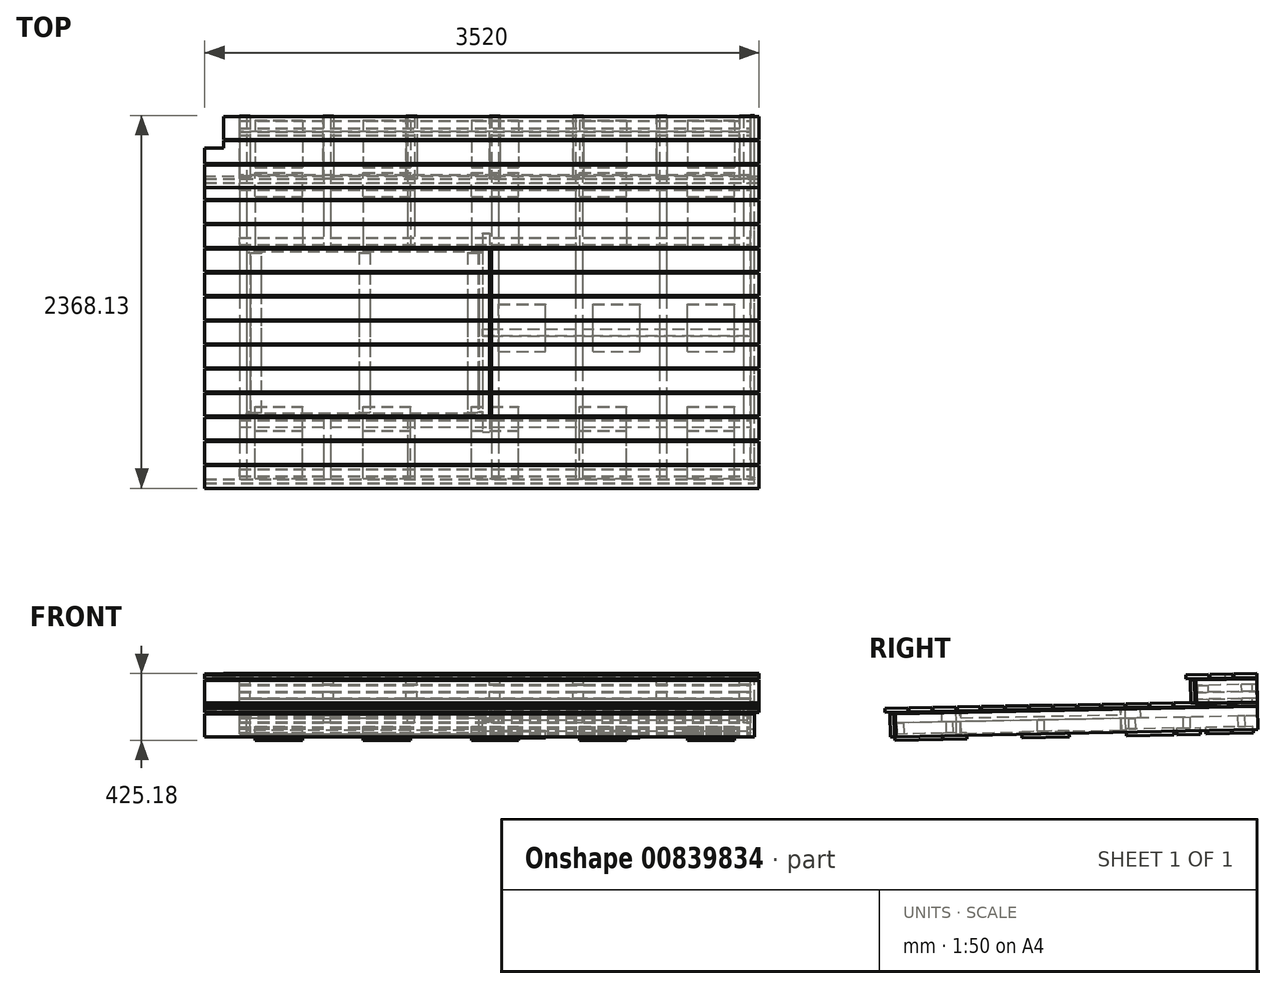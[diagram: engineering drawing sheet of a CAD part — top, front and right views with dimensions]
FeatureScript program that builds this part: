
annotation { "Feature Type Name" : "Feature", "Feature Type Description" : "" }
export const myFeature = defineFeature(function(context is Context, id is Id, definition is map)
    precondition{}
    {
        {
            var Q0;
            Q0=qCreatedBy(makeId("Top.planeOp"),FACE);
            var sketch = newSketch(context, id + "F0", { "sketchPlane" : qUnion([Q0])});
            skLineSegment(sketch, "E0", {"start": v(0, 0) * mm, "end": v(3520, 0) * mm, "construction": true});
            skSolve(sketch);
        }
        {
            var Q0;
            Q0=qCreatedBy(makeId("Top.planeOp"),FACE);
            var Q1;
            Q1=sQuery(id+"F0.wireOp",EDGE,"E0");
            cPlane(context, id + "F1", {"entities" : qUnion([Q0, Q1]), "cplaneType" : CPlaneType.LINE_ANGLE, "offset" : 25 * mm, "angle" : 1.15 * degree, "width" : 150 * mm, "height" : 150 * mm});
        }
        {
            var Q0;
            Q0=qCreatedBy(id+"F1.planeOp",FACE);
            var sketch = newSketch(context, id + "F2", { "sketchPlane" : qUnion([Q0])});
            skLineSegment(sketch, "E1.bottom", {"start": v(120, 0) * mm, "end": v(3520, 0) * mm});
            skLineSegment(sketch, "E1.top", {"start": v(120, 145) * mm, "end": v(3520, 145) * mm});
            skLineSegment(sketch, "E1.left", {"start": v(120, 0) * mm, "end": v(120, 145) * mm});
            skLineSegment(sketch, "E1.right", {"start": v(3520, 0) * mm, "end": v(3520, 145) * mm});
            skLineSegment(sketch, "E2.bottom", {"start": v(3520, 153) * mm, "end": v(120, 153) * mm});
            skLineSegment(sketch, "E2.top", {"start": v(3520, 298) * mm, "end": v(0, 298) * mm});
            skLineSegment(sketch, "E2.left", {"start": v(3520, 153) * mm, "end": v(3520, 298) * mm});
            skLineSegment(sketch, "E2.right", {"start": v(0, 200) * mm, "end": v(0, 298) * mm});
            skLineSegment(sketch, "E3.bottom", {"start": v(3520, 306) * mm, "end": v(0, 306) * mm});
            skLineSegment(sketch, "E3.top", {"start": v(3520, 451) * mm, "end": v(0, 451) * mm});
            skLineSegment(sketch, "E3.left", {"start": v(3520, 306) * mm, "end": v(3520, 451) * mm});
            skLineSegment(sketch, "E3.right", {"start": v(0, 306) * mm, "end": v(0, 451) * mm});
            skLineSegment(sketch, "E4", {"start": v(120, 153) * mm, "end": v(120, 200) * mm});
            skLineSegment(sketch, "E5", {"start": v(120, 200) * mm, "end": v(0, 200) * mm});
            skSolve(sketch);
        }
        {
            var Q0;
            Q0 = qSketchRegion(id + "F2", true);
            extrude(context, id + "F3", {"entities" : qUnion([Q0]), "depth" : 25 * mm, "offsetDistance" : 25 * mm});
        }
        {
            var Q0;
            Q0=makeQuery(id+"F3.opExtrude","CAP_FACE",FACE,{"disambiguationData":[OSD([sQuery(id+"F2.wireOp",EDGE,"E3.bottom"),sQuery(id+"F2.wireOp",EDGE,"E3.top"),sQuery(id+"F2.wireOp",EDGE,"E3.left"),sQuery(id+"F2.wireOp",EDGE,"E3.right")])],"isStart":false});
            var sketch = newSketch(context, id + "F4", { "sketchPlane" : qUnion([Q0])});
            skLineSegment(sketch, "E6.bottom", {"start": v(3465, 0) * mm, "end": v(3397, 0) * mm});
            skLineSegment(sketch, "E6.top", {"start": v(3465, 396) * mm, "end": v(3397, 396) * mm});
            skLineSegment(sketch, "E6.left", {"start": v(3465, 0) * mm, "end": v(3465, 396) * mm});
            skLineSegment(sketch, "E6.right", {"start": v(3397, 0) * mm, "end": v(3397, 396) * mm});
            skLineSegment(sketch, "E7.1.0.0", {"start": v(2935.5, 396) * mm, "end": v(2867.5, 396) * mm});
            skLineSegment(sketch, "E7.1.0.1", {"start": v(2935.5, 0) * mm, "end": v(2935.5, 396) * mm});
            skLineSegment(sketch, "E7.1.0.2", {"start": v(2867.5, 0) * mm, "end": v(2867.5, 396) * mm});
            skLineSegment(sketch, "E7.1.0.3", {"start": v(2935.5, 0) * mm, "end": v(2867.5, 0) * mm});
            skLineSegment(sketch, "E7.2.0.0", {"start": v(2406, 396) * mm, "end": v(2338, 396) * mm});
            skLineSegment(sketch, "E7.2.0.1", {"start": v(2406, 0) * mm, "end": v(2406, 396) * mm});
            skLineSegment(sketch, "E7.2.0.2", {"start": v(2338, 0) * mm, "end": v(2338, 396) * mm});
            skLineSegment(sketch, "E7.2.0.3", {"start": v(2406, 0) * mm, "end": v(2338, 0) * mm});
            skLineSegment(sketch, "E7.direction1", {"start": v(3397, 0) * mm, "end": v(2867.5, 0) * mm, "construction": true});
            skLineSegment(sketch, "E8.0.3.0", {"start": v(1876.5, 396) * mm, "end": v(1808.5, 396) * mm});
            skLineSegment(sketch, "E8.3.3.0", {"start": v(1876.5, 0) * mm, "end": v(1876.5, 396) * mm});
            skLineSegment(sketch, "E8.6.3.0", {"start": v(1808.5, 0) * mm, "end": v(1808.5, 396) * mm});
            skLineSegment(sketch, "E8.9.3.0", {"start": v(1876.5, 0) * mm, "end": v(1808.5, 0) * mm});
            skLineSegment(sketch, "E8.0.4.0", {"start": v(1347, 396) * mm, "end": v(1279, 396) * mm});
            skLineSegment(sketch, "E8.3.4.0", {"start": v(1347, 0) * mm, "end": v(1347, 396) * mm});
            skLineSegment(sketch, "E8.6.4.0", {"start": v(1279, 0) * mm, "end": v(1279, 396) * mm});
            skLineSegment(sketch, "E8.9.4.0", {"start": v(1347, 0) * mm, "end": v(1279, 0) * mm});
            skLineSegment(sketch, "E9.0.5.0", {"start": v(817.5, 396) * mm, "end": v(749.5, 396) * mm});
            skLineSegment(sketch, "E9.3.5.0", {"start": v(817.5, 0) * mm, "end": v(817.5, 396) * mm});
            skLineSegment(sketch, "E9.6.5.0", {"start": v(749.5, 0) * mm, "end": v(749.5, 396) * mm});
            skLineSegment(sketch, "E9.9.5.0", {"start": v(817.5, 0) * mm, "end": v(749.5, 0) * mm});
            skLineSegment(sketch, "E10.0.6.0", {"start": v(288, 396) * mm, "end": v(220, 396) * mm});
            skLineSegment(sketch, "E10.3.6.0", {"start": v(288, 0) * mm, "end": v(288, 396) * mm});
            skLineSegment(sketch, "E10.6.6.0", {"start": v(220, 0) * mm, "end": v(220, 396) * mm});
            skLineSegment(sketch, "E10.9.6.0", {"start": v(288, 0) * mm, "end": v(220, 0) * mm});
            skSolve(sketch);
        }
        {
            var Q0;
            Q0 = qSketchRegion(id + "F4", true);
            extrude(context, id + "F5", {"entities" : qUnion([Q0]), "depth" : 44 * mm, "offsetDistance" : 25 * mm});
        }
        {
            var Q0;
            Q0=makeQuery(id+"F5.opExtrude","CAP_FACE",FACE,{"disambiguationData":[OSD([sQuery(id+"F4.wireOp",EDGE,"E6.bottom"),sQuery(id+"F4.wireOp",EDGE,"E6.top"),sQuery(id+"F4.wireOp",EDGE,"E6.left"),sQuery(id+"F4.wireOp",EDGE,"E6.right")])],"isStart":false});
            var sketch = newSketch(context, id + "F6", { "sketchPlane" : qUnion([Q0])});
            skLineSegment(sketch, "E11.bottom", {"start": v(220, 30) * mm, "end": v(3465, 30) * mm});
            skLineSegment(sketch, "E11.top", {"start": v(220, 98) * mm, "end": v(3465, 98) * mm});
            skLineSegment(sketch, "E11.left", {"start": v(220, 30) * mm, "end": v(220, 98) * mm});
            skLineSegment(sketch, "E11.right", {"start": v(3465, 30) * mm, "end": v(3465, 98) * mm});
            skLineSegment(sketch, "E12.bottom", {"start": v(220, 376) * mm, "end": v(3465, 376) * mm});
            skLineSegment(sketch, "E12.top", {"start": v(220, 308) * mm, "end": v(3465, 308) * mm});
            skLineSegment(sketch, "E12.left", {"start": v(220, 376) * mm, "end": v(220, 308) * mm});
            skLineSegment(sketch, "E12.right", {"start": v(3465, 376) * mm, "end": v(3465, 308) * mm});
            skSolve(sketch);
        }
        {
            var Q0;
            Q0 = qSketchRegion(id + "F6", true);
            extrude(context, id + "F7", {"entities" : qUnion([Q0]), "depth" : 44 * mm, "offsetDistance" : 25 * mm});
        }
        {
            var Q0;
            Q0=makeQuery(id+"F7.opExtrude","CAP_FACE",FACE,{"disambiguationData":[OSD([sQuery(id+"F6.wireOp",EDGE,"E11.bottom"),sQuery(id+"F6.wireOp",EDGE,"E11.top"),sQuery(id+"F6.wireOp",EDGE,"E11.left"),sQuery(id+"F6.wireOp",EDGE,"E11.right")])],"isStart":false});
            var sketch = newSketch(context, id + "F8", { "sketchPlane" : qUnion([Q0])});
            skLineSegment(sketch, "E13.0.0", {"start": v(2867.5, 396) * mm, "end": v(2867.5, 0) * mm});
            skLineSegment(sketch, "E13.0.1", {"start": v(2867.5, 0) * mm, "end": v(2935.5, 0) * mm});
            skLineSegment(sketch, "E13.0.2", {"start": v(2935.5, 0) * mm, "end": v(2935.5, 396) * mm});
            skLineSegment(sketch, "E13.0.3", {"start": v(2935.5, 396) * mm, "end": v(2867.5, 396) * mm});
            skLineSegment(sketch, "E14.0.0", {"start": v(2338, 396) * mm, "end": v(2338, 0) * mm});
            skLineSegment(sketch, "E14.0.1", {"start": v(2338, 0) * mm, "end": v(2406, 0) * mm});
            skLineSegment(sketch, "E14.0.2", {"start": v(2406, 0) * mm, "end": v(2406, 396) * mm});
            skLineSegment(sketch, "E14.0.3", {"start": v(2406, 396) * mm, "end": v(2338, 396) * mm});
            skLineSegment(sketch, "E15.0.0", {"start": v(1808.5, 396) * mm, "end": v(1808.5, 0) * mm});
            skLineSegment(sketch, "E15.0.1", {"start": v(1808.5, 0) * mm, "end": v(1876.5, 0) * mm});
            skLineSegment(sketch, "E15.0.2", {"start": v(1876.5, 0) * mm, "end": v(1876.5, 396) * mm});
            skLineSegment(sketch, "E15.0.3", {"start": v(1876.5, 396) * mm, "end": v(1808.5, 396) * mm});
            skLineSegment(sketch, "E16.0.0", {"start": v(1279, 396) * mm, "end": v(1279, 0) * mm});
            skLineSegment(sketch, "E16.0.1", {"start": v(1279, 0) * mm, "end": v(1347, 0) * mm});
            skLineSegment(sketch, "E16.0.2", {"start": v(1347, 0) * mm, "end": v(1347, 396) * mm});
            skLineSegment(sketch, "E16.0.3", {"start": v(1347, 396) * mm, "end": v(1279, 396) * mm});
            skLineSegment(sketch, "E17.0.0", {"start": v(749.5, 396) * mm, "end": v(749.5, 0) * mm});
            skLineSegment(sketch, "E17.0.1", {"start": v(749.5, 0) * mm, "end": v(817.5, 0) * mm});
            skLineSegment(sketch, "E17.0.2", {"start": v(817.5, 0) * mm, "end": v(817.5, 396) * mm});
            skLineSegment(sketch, "E17.0.3", {"start": v(817.5, 396) * mm, "end": v(749.5, 396) * mm});
            skLineSegment(sketch, "E18.0.0", {"start": v(220, 396) * mm, "end": v(220, 0) * mm});
            skLineSegment(sketch, "E18.0.1", {"start": v(220, 0) * mm, "end": v(288, 0) * mm});
            skLineSegment(sketch, "E18.0.2", {"start": v(288, 0) * mm, "end": v(288, 396) * mm});
            skLineSegment(sketch, "E18.0.3", {"start": v(288, 396) * mm, "end": v(220, 396) * mm});
            skLineSegment(sketch, "E19.0.0", {"start": v(3465, 396) * mm, "end": v(3397, 396) * mm});
            skLineSegment(sketch, "E19.0.1", {"start": v(3397, 396) * mm, "end": v(3397, 0) * mm});
            skLineSegment(sketch, "E19.0.2", {"start": v(3397, 0) * mm, "end": v(3465, 0) * mm});
            skLineSegment(sketch, "E19.0.3", {"start": v(3465, 0) * mm, "end": v(3465, 396) * mm});
            skSolve(sketch);
        }
        {
            var Q0;
            Q0 = qSketchRegion(id + "F8", true);
            extrude(context, id + "F9", {"entities" : qUnion([Q0]), "depth" : 44 * mm, "offsetDistance" : 25 * mm});
        }
        {
            var Q0;
            Q0=makeQuery(id+"F9.opExtrude","CAP_FACE",FACE,{"disambiguationData":[OSD([sQuery(id+"F8.wireOp",EDGE,"E18.0.0"),sQuery(id+"F8.wireOp",EDGE,"E18.0.1"),sQuery(id+"F8.wireOp",EDGE,"E18.0.2"),sQuery(id+"F8.wireOp",EDGE,"E18.0.3")])],"isStart":false});
            var sketch = newSketch(context, id + "F10", { "sketchPlane" : qUnion([Q0])});
            skLineSegment(sketch, "E20.0.0", {"start": v(220, 376) * mm, "end": v(220, 308) * mm});
            skLineSegment(sketch, "E20.0.1", {"start": v(220, 308) * mm, "end": v(3465, 308) * mm});
            skLineSegment(sketch, "E20.0.2", {"start": v(3465, 308) * mm, "end": v(3465, 376) * mm});
            skLineSegment(sketch, "E20.0.3", {"start": v(3465, 376) * mm, "end": v(220, 376) * mm});
            skLineSegment(sketch, "E21.0.0", {"start": v(3465, 30) * mm, "end": v(3465, 98) * mm});
            skLineSegment(sketch, "E21.0.1", {"start": v(3465, 98) * mm, "end": v(220, 98) * mm});
            skLineSegment(sketch, "E21.0.2", {"start": v(220, 98) * mm, "end": v(220, 30) * mm});
            skLineSegment(sketch, "E21.0.3", {"start": v(220, 30) * mm, "end": v(3465, 30) * mm});
            skSolve(sketch);
        }
        {
            var Q0;
            Q0 = qSketchRegion(id + "F10", true);
            extrude(context, id + "F11", {"entities" : qUnion([Q0]), "depth" : 44 * mm, "offsetDistance" : 25 * mm});
        }
        {
            var Q0;
            Q0=makeQuery(id+"F5.opExtrude","SWEPT_FACE",FACE,{"disambiguationData":[OSD([sQuery(id+"F4.wireOp",EDGE,"E10.0.6.0")])]});
            var sketch = newSketch(context, id + "F12", { "sketchPlane" : qUnion([Q0])});
            skLineSegment(sketch, "E22.bottom", {"start": v(0, -180) * mm, "end": v(3520, -180) * mm});
            skLineSegment(sketch, "E22.top", {"start": v(0, -35) * mm, "end": v(3520, -35) * mm});
            skLineSegment(sketch, "E22.left", {"start": v(0, -180) * mm, "end": v(0, -35) * mm});
            skLineSegment(sketch, "E22.right", {"start": v(3520, -180) * mm, "end": v(3520, -35) * mm});
            skSolve(sketch);
        }
        {
            var Q0;
            Q0 = qSketchRegion(id + "F12", true);
            extrude(context, id + "F13", {"entities" : qUnion([Q0]), "depth" : 25 * mm, "offsetDistance" : 25 * mm});
        }
        {
            var Q0;
            Q0=makeQuery(id+"F11.opExtrude","CAP_FACE",FACE,{"disambiguationData":[OSD([sQuery(id+"F10.wireOp",EDGE,"E21.0.0"),sQuery(id+"F10.wireOp",EDGE,"E21.0.1"),sQuery(id+"F10.wireOp",EDGE,"E21.0.2"),sQuery(id+"F10.wireOp",EDGE,"E21.0.3")])],"isStart":false});
            var sketch = newSketch(context, id + "F14", { "sketchPlane" : qUnion([Q0])});
            skLineSegment(sketch, "E23.bottom", {"start": v(3465, 0) * mm, "end": v(3421, 0) * mm});
            skLineSegment(sketch, "E23.top", {"start": v(3465, 2310) * mm, "end": v(3421, 2310) * mm});
            skLineSegment(sketch, "E23.left", {"start": v(3465, 0) * mm, "end": v(3465, 2310) * mm});
            skLineSegment(sketch, "E23.right", {"start": v(3421, 0) * mm, "end": v(3421, 2310) * mm});
            skLineSegment(sketch, "E24.1.0.0", {"start": v(2931.5, 0) * mm, "end": v(2931.5, 2310) * mm});
            skLineSegment(sketch, "E24.1.0.1", {"start": v(2887.5, 0) * mm, "end": v(2887.5, 2310) * mm});
            skLineSegment(sketch, "E24.1.0.2", {"start": v(2931.5, 2310) * mm, "end": v(2887.5, 2310) * mm});
            skLineSegment(sketch, "E24.1.0.3", {"start": v(2931.5, 0) * mm, "end": v(2887.5, 0) * mm});
            skLineSegment(sketch, "E24.2.0.0", {"start": v(2398, 0) * mm, "end": v(2398, 2310) * mm});
            skLineSegment(sketch, "E24.2.0.1", {"start": v(2354, 0) * mm, "end": v(2354, 2310) * mm});
            skLineSegment(sketch, "E24.2.0.2", {"start": v(2398, 2310) * mm, "end": v(2354, 2310) * mm});
            skLineSegment(sketch, "E24.2.0.3", {"start": v(2398, 0) * mm, "end": v(2354, 0) * mm});
            skLineSegment(sketch, "E24.3.0.0", {"start": v(1864.5, 0) * mm, "end": v(1864.5, 2310) * mm});
            skLineSegment(sketch, "E24.3.0.1", {"start": v(1820.5, 0) * mm, "end": v(1820.5, 2310) * mm});
            skLineSegment(sketch, "E24.3.0.2", {"start": v(1864.5, 2310) * mm, "end": v(1820.5, 2310) * mm});
            skLineSegment(sketch, "E24.3.0.3", {"start": v(1864.5, 0) * mm, "end": v(1820.5, 0) * mm});
            skLineSegment(sketch, "E24.4.0.0", {"start": v(1331, 0) * mm, "end": v(1331, 839) * mm});
            skLineSegment(sketch, "E24.4.0.1", {"start": v(1287, 0) * mm, "end": v(1287, 839) * mm});
            skLineSegment(sketch, "E24.4.0.2", {"start": v(1331, 2310) * mm, "end": v(1287, 2310) * mm});
            skLineSegment(sketch, "E24.4.0.3", {"start": v(1331, 0) * mm, "end": v(1287, 0) * mm});
            skLineSegment(sketch, "E24.5.0.0", {"start": v(797.5, 0) * mm, "end": v(797.5, 839) * mm});
            skLineSegment(sketch, "E24.5.0.1", {"start": v(753.5, 0) * mm, "end": v(753.5, 839) * mm});
            skLineSegment(sketch, "E24.5.0.2", {"start": v(797.5, 2310) * mm, "end": v(753.5, 2310) * mm});
            skLineSegment(sketch, "E24.5.0.3", {"start": v(797.5, 0) * mm, "end": v(753.5, 0) * mm});
            skLineSegment(sketch, "E24.6.0.0", {"start": v(264, 0) * mm, "end": v(264, 2310) * mm});
            skLineSegment(sketch, "E24.6.0.1", {"start": v(220, 0) * mm, "end": v(220, 2310) * mm});
            skLineSegment(sketch, "E24.6.0.2", {"start": v(264, 2310) * mm, "end": v(220, 2310) * mm});
            skLineSegment(sketch, "E24.6.0.3", {"start": v(264, 0) * mm, "end": v(220, 0) * mm});
            skLineSegment(sketch, "E24.direction1", {"start": v(3421, 0) * mm, "end": v(2887.5, 0) * mm, "construction": true});
            skLineSegment(sketch, "E25.bottom", {"start": v(753.5, 1914) * mm, "end": v(797.5, 1914) * mm});
            skLineSegment(sketch, "E25.top", {"start": v(753.5, 839) * mm, "end": v(797.5, 839) * mm});
            skLineSegment(sketch, "E26.trimOffspring", {"start": v(1331, 1914) * mm, "end": v(1331, 2310) * mm});
            skLineSegment(sketch, "E27.trimOffspring", {"start": v(1287, 1914) * mm, "end": v(1287, 2310) * mm});
            skLineSegment(sketch, "E28.trimOffspring", {"start": v(797.5, 1914) * mm, "end": v(797.5, 2310) * mm});
            skLineSegment(sketch, "E29.trimOffspring", {"start": v(753.5, 1914) * mm, "end": v(753.5, 2310) * mm});
            skLineSegment(sketch, "E30.trimOffspring", {"start": v(1287, 1914) * mm, "end": v(1331, 1914) * mm});
            skLineSegment(sketch, "E31.trimOffspring", {"start": v(1287, 839) * mm, "end": v(1331, 839) * mm});
            skSolve(sketch);
        }
        {
            var Q0;
            Q0 = qSketchRegion(id + "F14", true);
            extrude(context, id + "F15", {"entities" : qUnion([Q0]), "depth" : 68 * mm, "offsetDistance" : 25 * mm});
        }
        {
            var Q0;
            Q0=makeQuery(id+"F15.opExtrude","CAP_FACE",FACE,{"disambiguationData":[OSD([sQuery(id+"F14.wireOp",EDGE,"E24.3.0.0"),sQuery(id+"F14.wireOp",EDGE,"E24.3.0.1"),sQuery(id+"F14.wireOp",EDGE,"E24.3.0.2"),sQuery(id+"F14.wireOp",EDGE,"E24.3.0.3")])],"isStart":false});
            var sketch = newSketch(context, id + "F16", { "sketchPlane" : qUnion([Q0])});
            skLineSegment(sketch, "E32.bottom", {"start": v(220, 2290) * mm, "end": v(3465, 2290) * mm});
            skLineSegment(sketch, "E32.top", {"start": v(220, 2246) * mm, "end": v(3465, 2246) * mm});
            skLineSegment(sketch, "E32.left", {"start": v(220, 2290) * mm, "end": v(220, 2246) * mm});
            skLineSegment(sketch, "E32.right", {"start": v(3465, 2290) * mm, "end": v(3465, 2246) * mm});
            skLineSegment(sketch, "E33.bottom", {"start": v(220, 1934) * mm, "end": v(3465, 1934) * mm});
            skLineSegment(sketch, "E33.top", {"start": v(220, 1978) * mm, "end": v(3465, 1978) * mm});
            skLineSegment(sketch, "E33.left", {"start": v(220, 1934) * mm, "end": v(220, 1978) * mm});
            skLineSegment(sketch, "E33.right", {"start": v(3465, 1934) * mm, "end": v(3465, 1978) * mm});
            skLineSegment(sketch, "E34.bottom", {"start": v(220, 819) * mm, "end": v(3465, 819) * mm});
            skLineSegment(sketch, "E34.top", {"start": v(220, 775) * mm, "end": v(3465, 775) * mm});
            skLineSegment(sketch, "E34.left", {"start": v(220, 819) * mm, "end": v(220, 775) * mm});
            skLineSegment(sketch, "E34.right", {"start": v(3465, 819) * mm, "end": v(3465, 775) * mm});
            skLineSegment(sketch, "E35.bottom", {"start": v(220, 80) * mm, "end": v(3465, 80) * mm});
            skLineSegment(sketch, "E35.top", {"start": v(220, 124) * mm, "end": v(3465, 124) * mm});
            skLineSegment(sketch, "E35.left", {"start": v(220, 80) * mm, "end": v(220, 124) * mm});
            skLineSegment(sketch, "E35.right", {"start": v(3465, 80) * mm, "end": v(3465, 124) * mm});
            skLineSegment(sketch, "E36.bottom", {"start": v(1765.5, 1398.5) * mm, "end": v(3465, 1398.5) * mm});
            skLineSegment(sketch, "E36.top", {"start": v(1765.5, 1354.5) * mm, "end": v(3465, 1354.5) * mm});
            skLineSegment(sketch, "E36.left", {"start": v(1765.5, 1398.5) * mm, "end": v(1765.5, 1354.5) * mm});
            skLineSegment(sketch, "E36.right", {"start": v(3465, 1398.5) * mm, "end": v(3465, 1354.5) * mm});
            skLineSegment(sketch, "E37", {"start": v(1765.5, 1354.5) * mm, "end": v(1765.5, 819) * mm, "construction": true});
            skLineSegment(sketch, "E38", {"start": v(1765.5, 1398.5) * mm, "end": v(1765.5, 1934) * mm, "construction": true});
            skLineSegment(sketch, "E39.bottom", {"start": v(220, 471.5) * mm, "end": v(3465, 471.5) * mm});
            skLineSegment(sketch, "E39.top", {"start": v(220, 427.5) * mm, "end": v(3465, 427.5) * mm});
            skLineSegment(sketch, "E39.left", {"start": v(220, 471.5) * mm, "end": v(220, 427.5) * mm});
            skLineSegment(sketch, "E39.right", {"start": v(3465, 471.5) * mm, "end": v(3465, 427.5) * mm});
            skLineSegment(sketch, "E40", {"start": v(220, 427.5) * mm, "end": v(220, 124) * mm, "construction": true});
            skLineSegment(sketch, "E41", {"start": v(220, 775) * mm, "end": v(220, 471.5) * mm, "construction": true});
            skSolve(sketch);
        }
        {
            var Q0;
            Q0 = qSketchRegion(id + "F16", true);
            extrude(context, id + "F17", {"entities" : qUnion([Q0]), "depth" : 68 * mm, "offsetDistance" : 25 * mm});
        }
        {
            var Q0;
            Q0=makeQuery(id+"F15.opExtrude","CAP_FACE",FACE,{"disambiguationData":[OSD([sQuery(id+"F14.wireOp",EDGE,"E23.bottom"),sQuery(id+"F14.wireOp",EDGE,"E23.top"),sQuery(id+"F14.wireOp",EDGE,"E23.left"),sQuery(id+"F14.wireOp",EDGE,"E23.right")])],"isStart":true});
            var sketch = newSketch(context, id + "F18", { "sketchPlane" : qUnion([Q0])});
            skLineSegment(sketch, "E42.bottom", {"start": v(3520, -384) * mm, "end": v(0, -384) * mm});
            skLineSegment(sketch, "E42.top", {"start": v(3520, -529) * mm, "end": v(0, -529) * mm});
            skLineSegment(sketch, "E42.left", {"start": v(3520, -384) * mm, "end": v(3520, -529) * mm});
            skLineSegment(sketch, "E42.right", {"start": v(0, -384) * mm, "end": v(0, -529) * mm});
            skLineSegment(sketch, "E43.bottom", {"start": v(3520, -537) * mm, "end": v(0, -537) * mm});
            skLineSegment(sketch, "E43.top", {"start": v(3520, -682) * mm, "end": v(0, -682) * mm});
            skLineSegment(sketch, "E43.left", {"start": v(3520, -537) * mm, "end": v(3520, -682) * mm});
            skLineSegment(sketch, "E43.right", {"start": v(0, -537) * mm, "end": v(0, -682) * mm});
            skLineSegment(sketch, "E44.bottom", {"start": v(3520, -690) * mm, "end": v(0, -690) * mm});
            skLineSegment(sketch, "E44.top", {"start": v(3520, -835) * mm, "end": v(0, -835) * mm});
            skLineSegment(sketch, "E44.left", {"start": v(3520, -690) * mm, "end": v(3520, -835) * mm});
            skLineSegment(sketch, "E44.right", {"start": v(0, -690) * mm, "end": v(0, -835) * mm});
            skLineSegment(sketch, "E45.bottom", {"start": v(3520, -843) * mm, "end": v(1820.5, -843) * mm});
            skLineSegment(sketch, "E45.top", {"start": v(3520, -988) * mm, "end": v(1820.5, -988) * mm});
            skLineSegment(sketch, "E45.left", {"start": v(3520, -843) * mm, "end": v(3520, -988) * mm});
            skLineSegment(sketch, "E45.right", {"start": v(1820.5, -843) * mm, "end": v(1820.5, -988) * mm});
            skLineSegment(sketch, "E46.bottom", {"start": v(3520, -996) * mm, "end": v(1820.5, -996) * mm});
            skLineSegment(sketch, "E46.top", {"start": v(3520, -1141) * mm, "end": v(1820.5, -1141) * mm});
            skLineSegment(sketch, "E46.left", {"start": v(3520, -996) * mm, "end": v(3520, -1141) * mm});
            skLineSegment(sketch, "E46.right", {"start": v(1820.5, -996) * mm, "end": v(1820.5, -1141) * mm});
            skLineSegment(sketch, "E47.bottom", {"start": v(3520, -1149) * mm, "end": v(1820.5, -1149) * mm});
            skLineSegment(sketch, "E47.top", {"start": v(3520, -1294) * mm, "end": v(1820.5, -1294) * mm});
            skLineSegment(sketch, "E47.left", {"start": v(3520, -1149) * mm, "end": v(3520, -1294) * mm});
            skLineSegment(sketch, "E47.right", {"start": v(1820.5, -1149) * mm, "end": v(1820.5, -1294) * mm});
            skLineSegment(sketch, "E48.bottom", {"start": v(3520, -1302) * mm, "end": v(1820.5, -1302) * mm});
            skLineSegment(sketch, "E48.top", {"start": v(3520, -1447) * mm, "end": v(1820.5, -1447) * mm});
            skLineSegment(sketch, "E48.left", {"start": v(3520, -1302) * mm, "end": v(3520, -1447) * mm});
            skLineSegment(sketch, "E48.right", {"start": v(1820.5, -1302) * mm, "end": v(1820.5, -1447) * mm});
            skLineSegment(sketch, "E49.bottom", {"start": v(3520, -1455) * mm, "end": v(1820.5, -1455) * mm});
            skLineSegment(sketch, "E49.top", {"start": v(3520, -1600) * mm, "end": v(1820.5, -1600) * mm});
            skLineSegment(sketch, "E49.left", {"start": v(3520, -1455) * mm, "end": v(3520, -1600) * mm});
            skLineSegment(sketch, "E49.right", {"start": v(1820.5, -1455) * mm, "end": v(1820.5, -1600) * mm});
            skLineSegment(sketch, "E50.bottom", {"start": v(3520, -1608) * mm, "end": v(1820.5, -1608) * mm});
            skLineSegment(sketch, "E50.top", {"start": v(3520, -1753) * mm, "end": v(1820.5, -1753) * mm});
            skLineSegment(sketch, "E50.left", {"start": v(3520, -1608) * mm, "end": v(3520, -1753) * mm});
            skLineSegment(sketch, "E50.right", {"start": v(1820.5, -1608) * mm, "end": v(1820.5, -1753) * mm});
            skLineSegment(sketch, "E51.bottom", {"start": v(3520, -1761) * mm, "end": v(1820.5, -1761) * mm});
            skLineSegment(sketch, "E51.top", {"start": v(3520, -1906) * mm, "end": v(1820.5, -1906) * mm});
            skLineSegment(sketch, "E51.left", {"start": v(3520, -1761) * mm, "end": v(3520, -1906) * mm});
            skLineSegment(sketch, "E51.right", {"start": v(1820.5, -1761) * mm, "end": v(1820.5, -1906) * mm});
            skLineSegment(sketch, "E52.bottom", {"start": v(3520, -1914) * mm, "end": v(0, -1914) * mm});
            skLineSegment(sketch, "E52.top", {"start": v(3520, -2059) * mm, "end": v(0, -2059) * mm});
            skLineSegment(sketch, "E52.left", {"start": v(3520, -1914) * mm, "end": v(3520, -2059) * mm});
            skLineSegment(sketch, "E52.right", {"start": v(0, -1914) * mm, "end": v(0, -2059) * mm});
            skLineSegment(sketch, "E53.bottom", {"start": v(3520, -2067) * mm, "end": v(0, -2067) * mm});
            skLineSegment(sketch, "E53.top", {"start": v(3520, -2212) * mm, "end": v(0, -2212) * mm});
            skLineSegment(sketch, "E53.left", {"start": v(3520, -2067) * mm, "end": v(3520, -2212) * mm});
            skLineSegment(sketch, "E53.right", {"start": v(0, -2067) * mm, "end": v(0, -2212) * mm});
            skLineSegment(sketch, "E54.bottom", {"start": v(3520, -2220) * mm, "end": v(0, -2220) * mm});
            skLineSegment(sketch, "E54.top", {"start": v(3520, -2365) * mm, "end": v(0, -2365) * mm});
            skLineSegment(sketch, "E54.left", {"start": v(3520, -2220) * mm, "end": v(3520, -2365) * mm});
            skLineSegment(sketch, "E54.right", {"start": v(0, -2220) * mm, "end": v(0, -2365) * mm});
            skSolve(sketch);
        }
        {
            var Q0;
            Q0 = qSketchRegion(id + "F18", true);
            extrude(context, id + "F19", {"entities" : qUnion([Q0]), "depth" : 25 * mm, "offsetDistance" : 25 * mm});
        }
        {
            var Q0;
            Q0=makeQuery(id+"F17.opExtrude","CAP_FACE",FACE,{"disambiguationData":[OSD([sQuery(id+"F16.wireOp",EDGE,"E36.bottom"),sQuery(id+"F16.wireOp",EDGE,"E36.top"),sQuery(id+"F16.wireOp",EDGE,"E36.left"),sQuery(id+"F16.wireOp",EDGE,"E36.right")])],"isStart":true});
            var sketch = newSketch(context, id + "F20", { "sketchPlane" : qUnion([Q0])});
            skLineSegment(sketch, "E55.bottom", {"start": v(1765.5, -745) * mm, "end": v(1809.5, -745) * mm});
            skLineSegment(sketch, "E55.top", {"start": v(1765.5, -2008) * mm, "end": v(1809.5, -2008) * mm});
            skLineSegment(sketch, "E55.left", {"start": v(1765.5, -745) * mm, "end": v(1765.5, -2008) * mm});
            skLineSegment(sketch, "E55.right", {"start": v(1809.5, -745) * mm, "end": v(1809.5, -2008) * mm});
            skSolve(sketch);
        }
        {
            var Q0;
            Q0 = qSketchRegion(id + "F20", true);
            extrude(context, id + "F21", {"entities" : qUnion([Q0]), "depth" : 68 * mm, "offsetDistance" : 25 * mm});
        }
        {
            var Q0;
            Q0=makeQuery(id+"F21.opExtrude","CAP_FACE",FACE,{"disambiguationData":[OSD([sQuery(id+"F20.wireOp",EDGE,"E55.bottom"),sQuery(id+"F20.wireOp",EDGE,"E55.top"),sQuery(id+"F20.wireOp",EDGE,"E55.left"),sQuery(id+"F20.wireOp",EDGE,"E55.right")])],"isStart":false});
            var sketch = newSketch(context, id + "F22", { "sketchPlane" : qUnion([Q0])});
            skLineSegment(sketch, "E56.bottom", {"start": v(1765.5, -839) * mm, "end": v(264, -839) * mm});
            skLineSegment(sketch, "E56.top", {"start": v(1765.5, -864) * mm, "end": v(264, -864) * mm});
            skLineSegment(sketch, "E56.left", {"start": v(1765.5, -839) * mm, "end": v(1765.5, -864) * mm});
            skLineSegment(sketch, "E56.right", {"start": v(264, -839) * mm, "end": v(264, -864) * mm});
            skLineSegment(sketch, "E57.bottom", {"start": v(289, -869) * mm, "end": v(264, -869) * mm});
            skLineSegment(sketch, "E57.top", {"start": v(289, -1884) * mm, "end": v(264, -1884) * mm});
            skLineSegment(sketch, "E57.left", {"start": v(289, -869) * mm, "end": v(289, -1884) * mm});
            skLineSegment(sketch, "E57.right", {"start": v(264, -869) * mm, "end": v(264, -1884) * mm});
            skLineSegment(sketch, "E58.bottom", {"start": v(264, -1914) * mm, "end": v(1765.5, -1914) * mm});
            skLineSegment(sketch, "E58.top", {"start": v(264, -1889) * mm, "end": v(1765.5, -1889) * mm});
            skLineSegment(sketch, "E58.left", {"start": v(264, -1914) * mm, "end": v(264, -1889) * mm});
            skLineSegment(sketch, "E58.right", {"start": v(1765.5, -1914) * mm, "end": v(1765.5, -1889) * mm});
            skLineSegment(sketch, "E59.bottom", {"start": v(1765.5, -869) * mm, "end": v(1740.5, -869) * mm});
            skLineSegment(sketch, "E59.top", {"start": v(1765.5, -1884) * mm, "end": v(1740.5, -1884) * mm});
            skLineSegment(sketch, "E59.left", {"start": v(1765.5, -869) * mm, "end": v(1765.5, -1884) * mm});
            skLineSegment(sketch, "E59.right", {"start": v(1740.5, -869) * mm, "end": v(1740.5, -1884) * mm});
            skSolve(sketch);
        }
        {
            var Q0;
            Q0 = qSketchRegion(id + "F22", true);
            extrude(context, id + "F23", {"entities" : qUnion([Q0]), "oppositeDirection" : true, "depth" : 145 * mm, "offsetDistance" : 25 * mm});
        }
        {
            var Q0;
            Q0=makeQuery(id+"F21.opExtrude","CAP_FACE",FACE,{"disambiguationData":[OSD([sQuery(id+"F20.wireOp",EDGE,"E55.bottom"),sQuery(id+"F20.wireOp",EDGE,"E55.top"),sQuery(id+"F20.wireOp",EDGE,"E55.left"),sQuery(id+"F20.wireOp",EDGE,"E55.right")])],"isStart":false});
            var sketch = newSketch(context, id + "F24", { "sketchPlane" : qUnion([Q0])});
            skLineSegment(sketch, "E60.bottom", {"start": v(0, -843) * mm, "end": v(1809.5, -843) * mm});
            skLineSegment(sketch, "E60.top", {"start": v(0, -988) * mm, "end": v(1809.5, -988) * mm});
            skLineSegment(sketch, "E60.left", {"start": v(0, -843) * mm, "end": v(0, -988) * mm});
            skLineSegment(sketch, "E60.right", {"start": v(1809.5, -843) * mm, "end": v(1809.5, -988) * mm});
            skLineSegment(sketch, "E61.0.1.0", {"start": v(0, -996) * mm, "end": v(0, -1141) * mm});
            skLineSegment(sketch, "E61.0.1.1", {"start": v(0, -1141) * mm, "end": v(1809.5, -1141) * mm});
            skLineSegment(sketch, "E61.0.1.2", {"start": v(1809.5, -996) * mm, "end": v(1809.5, -1141) * mm});
            skLineSegment(sketch, "E61.0.1.3", {"start": v(0, -996) * mm, "end": v(1809.5, -996) * mm});
            skLineSegment(sketch, "E61.0.2.0", {"start": v(0, -1149) * mm, "end": v(0, -1294) * mm});
            skLineSegment(sketch, "E61.0.2.1", {"start": v(0, -1294) * mm, "end": v(1809.5, -1294) * mm});
            skLineSegment(sketch, "E61.0.2.2", {"start": v(1809.5, -1149) * mm, "end": v(1809.5, -1294) * mm});
            skLineSegment(sketch, "E61.0.2.3", {"start": v(0, -1149) * mm, "end": v(1809.5, -1149) * mm});
            skLineSegment(sketch, "E61.0.3.0", {"start": v(0, -1302) * mm, "end": v(0, -1447) * mm});
            skLineSegment(sketch, "E61.0.3.1", {"start": v(0, -1447) * mm, "end": v(1809.5, -1447) * mm});
            skLineSegment(sketch, "E61.0.3.2", {"start": v(1809.5, -1302) * mm, "end": v(1809.5, -1447) * mm});
            skLineSegment(sketch, "E61.0.3.3", {"start": v(0, -1302) * mm, "end": v(1809.5, -1302) * mm});
            skLineSegment(sketch, "E61.0.4.0", {"start": v(0, -1455) * mm, "end": v(0, -1600) * mm});
            skLineSegment(sketch, "E61.0.4.1", {"start": v(0, -1600) * mm, "end": v(1809.5, -1600) * mm});
            skLineSegment(sketch, "E61.0.4.2", {"start": v(1809.5, -1455) * mm, "end": v(1809.5, -1600) * mm});
            skLineSegment(sketch, "E61.0.4.3", {"start": v(0, -1455) * mm, "end": v(1809.5, -1455) * mm});
            skLineSegment(sketch, "E61.0.5.0", {"start": v(0, -1608) * mm, "end": v(0, -1753) * mm});
            skLineSegment(sketch, "E61.0.5.1", {"start": v(0, -1753) * mm, "end": v(1809.5, -1753) * mm});
            skLineSegment(sketch, "E61.0.5.2", {"start": v(1809.5, -1608) * mm, "end": v(1809.5, -1753) * mm});
            skLineSegment(sketch, "E61.0.5.3", {"start": v(0, -1608) * mm, "end": v(1809.5, -1608) * mm});
            skLineSegment(sketch, "E61.0.6.0", {"start": v(0, -1761) * mm, "end": v(0, -1906) * mm});
            skLineSegment(sketch, "E61.0.6.1", {"start": v(0, -1906) * mm, "end": v(1809.5, -1906) * mm});
            skLineSegment(sketch, "E61.0.6.2", {"start": v(1809.5, -1761) * mm, "end": v(1809.5, -1906) * mm});
            skLineSegment(sketch, "E61.0.6.3", {"start": v(0, -1761) * mm, "end": v(1809.5, -1761) * mm});
            skLineSegment(sketch, "E61.direction1", {"start": v(0, -988) * mm, "end": v(0.5, -988) * mm, "construction": true});
            skLineSegment(sketch, "E61.direction2", {"start": v(0, -988) * mm, "end": v(0, -1141) * mm, "construction": true});
            skSolve(sketch);
        }
        {
            var Q0;
            Q0 = qSketchRegion(id + "F24", true);
            extrude(context, id + "F25", {"entities" : qUnion([Q0]), "depth" : 25 * mm, "offsetDistance" : 25 * mm});
        }
        {
            var Q0;
            Q0=makeQuery(id+"F25.opExtrude","CAP_FACE",FACE,{"disambiguationData":[OSD([sQuery(id+"F24.wireOp",EDGE,"E61.0.4.0"),sQuery(id+"F24.wireOp",EDGE,"E61.0.4.1"),sQuery(id+"F24.wireOp",EDGE,"E61.0.4.2"),sQuery(id+"F24.wireOp",EDGE,"E61.0.4.3")])],"isStart":true});
            var sketch = newSketch(context, id + "F26", { "sketchPlane" : qUnion([Q0])});
            skLineSegment(sketch, "E62.bottom", {"start": v(294, 1884) * mm, "end": v(362, 1884) * mm});
            skLineSegment(sketch, "E62.top", {"start": v(294, 869) * mm, "end": v(362, 869) * mm});
            skLineSegment(sketch, "E62.left", {"start": v(294, 1884) * mm, "end": v(294, 869) * mm});
            skLineSegment(sketch, "E62.right", {"start": v(362, 1884) * mm, "end": v(362, 869) * mm});
            skLineSegment(sketch, "E63.bottom", {"start": v(980.75, 869) * mm, "end": v(1048.75, 869) * mm});
            skLineSegment(sketch, "E63.top", {"start": v(980.75, 1884) * mm, "end": v(1048.75, 1884) * mm});
            skLineSegment(sketch, "E63.left", {"start": v(980.75, 869) * mm, "end": v(980.75, 1884) * mm});
            skLineSegment(sketch, "E63.right", {"start": v(1048.75, 869) * mm, "end": v(1048.75, 1884) * mm});
            skLineSegment(sketch, "E64.bottom", {"start": v(1667.5, 869) * mm, "end": v(1735.5, 869) * mm});
            skLineSegment(sketch, "E64.top", {"start": v(1667.5, 1884) * mm, "end": v(1735.5, 1884) * mm});
            skLineSegment(sketch, "E64.left", {"start": v(1667.5, 869) * mm, "end": v(1667.5, 1884) * mm});
            skLineSegment(sketch, "E64.right", {"start": v(1735.5, 869) * mm, "end": v(1735.5, 1884) * mm});
            skLineSegment(sketch, "E65", {"start": v(362, 1884) * mm, "end": v(980.75, 1884) * mm, "construction": true});
            skLineSegment(sketch, "E66", {"start": v(1048.75, 1884) * mm, "end": v(1667.5, 1884) * mm, "construction": true});
            skSolve(sketch);
        }
        {
            var Q0;
            Q0 = qSketchRegion(id + "F26", true);
            extrude(context, id + "F27", {"entities" : qUnion([Q0]), "depth" : 44 * mm, "offsetDistance" : 25 * mm});
        }
        {
            var Q0;
            Q0=makeQuery(id+"F15.opExtrude","SWEPT_FACE",FACE,{"disambiguationData":[OSD([sQuery(id+"F14.wireOp",EDGE,"E23.top")])]});
            var sketch = newSketch(context, id + "F28", { "sketchPlane" : qUnion([Q0])});
            skLineSegment(sketch, "E67.bottom", {"start": v(0, -211) * mm, "end": v(3490, -211) * mm});
            skLineSegment(sketch, "E67.top", {"start": v(0, -356) * mm, "end": v(3490, -356) * mm});
            skLineSegment(sketch, "E67.left", {"start": v(0, -211) * mm, "end": v(0, -356) * mm});
            skLineSegment(sketch, "E67.right", {"start": v(3490, -356) * mm, "end": v(3490, -211) * mm});
            skSolve(sketch);
        }
        {
            var Q0;
            Q0 = qSketchRegion(id + "F28", true);
            extrude(context, id + "F29", {"entities" : qUnion([Q0]), "depth" : 25 * mm, "offsetDistance" : 25 * mm});
        }
        {
            var Q0;
            Q0=makeQuery(id+"F17.opExtrude","SWEPT_FACE",FACE,{"disambiguationData":[OSD([sQuery(id+"F16.wireOp",EDGE,"E32.right")])]});
            var sketch = newSketch(context, id + "F30", { "sketchPlane" : qUnion([Q0])});
            skLineSegment(sketch, "E68.bottom", {"start": v(-2292.4, -402.09) * mm, "end": v(7.14, -355.93) * mm});
            skLineSegment(sketch, "E68.top", {"start": v(-2295.3, -257.12) * mm, "end": v(4.23, -210.96) * mm});
            skLineSegment(sketch, "E68.left", {"start": v(-2292.4, -402.09) * mm, "end": v(-2295.3, -257.12) * mm});
            skLineSegment(sketch, "E68.right", {"start": v(7.14, -355.93) * mm, "end": v(4.23, -210.96) * mm});
            skLineSegment(sketch, "E69.bottom", {"start": v(-382.3, -187.71) * mm, "end": v(2.91, -179.98) * mm});
            skLineSegment(sketch, "E69.top", {"start": v(-385.22, -42.74) * mm, "end": v(0, -35) * mm});
            skLineSegment(sketch, "E69.left", {"start": v(-382.3, -187.71) * mm, "end": v(-385.22, -42.74) * mm});
            skLineSegment(sketch, "E69.right", {"start": v(2.91, -179.98) * mm, "end": v(0, -35) * mm});
            skLineSegment(sketch, "E70.bottom", {"start": v(-382.2, -192.7) * mm, "end": v(3.01, -184.98) * mm});
            skLineSegment(sketch, "E70.top", {"start": v(-381.79, -213.7) * mm, "end": v(3.43, -205.97) * mm});
            skLineSegment(sketch, "E70.left", {"start": v(-382.2, -192.7) * mm, "end": v(-381.79, -213.7) * mm});
            skLineSegment(sketch, "E70.right", {"start": v(3.01, -184.98) * mm, "end": v(3.43, -205.97) * mm});
            skSolve(sketch);
        }
        {
            var Q0;
            Q0 = qSketchRegion(id + "F30", true);
            extrude(context, id + "F31", {"entities" : qUnion([Q0]), "depth" : 25 * mm, "offsetDistance" : 25 * mm});
        }
        {
            var Q0;
            Q0=makeQuery(id+"F17.opExtrude","CAP_FACE",FACE,{"disambiguationData":[OSD([sQuery(id+"F16.wireOp",EDGE,"E32.bottom"),sQuery(id+"F16.wireOp",EDGE,"E32.top"),sQuery(id+"F16.wireOp",EDGE,"E32.left"),sQuery(id+"F16.wireOp",EDGE,"E32.right")])],"isStart":false});
            var sketch = newSketch(context, id + "F32", { "sketchPlane" : qUnion([Q0])});
            skLineSegment(sketch, "E71.bottom", {"start": v(320, 2305) * mm, "end": v(620, 2305) * mm});
            skLineSegment(sketch, "E71.top", {"start": v(320, 2005) * mm, "end": v(620, 2005) * mm});
            skLineSegment(sketch, "E71.left", {"start": v(320, 2305) * mm, "end": v(320, 2005) * mm});
            skLineSegment(sketch, "E71.right", {"start": v(620, 2305) * mm, "end": v(620, 2005) * mm});
            skLineSegment(sketch, "E72.bottom", {"start": v(1864.5, 1498.5) * mm, "end": v(2164.5, 1498.5) * mm});
            skLineSegment(sketch, "E72.top", {"start": v(1864.5, 1198.5) * mm, "end": v(2164.5, 1198.5) * mm});
            skLineSegment(sketch, "E72.left", {"start": v(1864.5, 1498.5) * mm, "end": v(1864.5, 1198.5) * mm});
            skLineSegment(sketch, "E72.right", {"start": v(2164.5, 1498.5) * mm, "end": v(2164.5, 1198.5) * mm});
            skLineSegment(sketch, "E73.bottom", {"start": v(3065, 1498.5) * mm, "end": v(3365, 1498.5) * mm});
            skLineSegment(sketch, "E73.top", {"start": v(3065, 1198.5) * mm, "end": v(3365, 1198.5) * mm});
            skLineSegment(sketch, "E73.left", {"start": v(3065, 1498.5) * mm, "end": v(3065, 1198.5) * mm});
            skLineSegment(sketch, "E73.right", {"start": v(3365, 1498.5) * mm, "end": v(3365, 1198.5) * mm});
            skLineSegment(sketch, "E74.bottom", {"start": v(320, 30) * mm, "end": v(620, 30) * mm});
            skLineSegment(sketch, "E74.top", {"start": v(320, 330) * mm, "end": v(620, 330) * mm});
            skLineSegment(sketch, "E74.left", {"start": v(320, 30) * mm, "end": v(320, 330) * mm});
            skLineSegment(sketch, "E74.right", {"start": v(620, 30) * mm, "end": v(620, 330) * mm});
            skLineSegment(sketch, "E75.bottom", {"start": v(2464.75, 1498.5) * mm, "end": v(2764.75, 1498.5) * mm});
            skLineSegment(sketch, "E75.top", {"start": v(2464.75, 1198.5) * mm, "end": v(2764.75, 1198.5) * mm});
            skLineSegment(sketch, "E75.left", {"start": v(2464.75, 1498.5) * mm, "end": v(2464.75, 1198.5) * mm});
            skLineSegment(sketch, "E75.right", {"start": v(2764.75, 1498.5) * mm, "end": v(2764.75, 1198.5) * mm});
            skLineSegment(sketch, "E76", {"start": v(2164.5, 1498.5) * mm, "end": v(2464.75, 1498.5) * mm, "construction": true});
            skLineSegment(sketch, "E77", {"start": v(3065, 1498.5) * mm, "end": v(2764.75, 1498.5) * mm, "construction": true});
            skLineSegment(sketch, "E78.bottom", {"start": v(320, 534) * mm, "end": v(620, 534) * mm});
            skLineSegment(sketch, "E78.top", {"start": v(320, 834) * mm, "end": v(620, 834) * mm});
            skLineSegment(sketch, "E78.left", {"start": v(320, 534) * mm, "end": v(320, 834) * mm});
            skLineSegment(sketch, "E78.right", {"start": v(620, 534) * mm, "end": v(620, 834) * mm});
            skLineSegment(sketch, "E79.1.0.0", {"start": v(1306.25, 534) * mm, "end": v(1306.25, 834) * mm});
            skLineSegment(sketch, "E79.1.0.1", {"start": v(1306.25, 30) * mm, "end": v(1306.25, 330) * mm});
            skLineSegment(sketch, "E79.1.0.2", {"start": v(1006.25, 834) * mm, "end": v(1306.25, 834) * mm});
            skLineSegment(sketch, "E79.1.0.3", {"start": v(1006.25, 534) * mm, "end": v(1006.25, 834) * mm});
            skLineSegment(sketch, "E79.1.0.4", {"start": v(1006.25, 30) * mm, "end": v(1306.25, 30) * mm});
            skLineSegment(sketch, "E79.1.0.5", {"start": v(1006.25, 330) * mm, "end": v(1306.25, 330) * mm});
            skLineSegment(sketch, "E79.1.0.6", {"start": v(1006.25, 30) * mm, "end": v(1006.25, 330) * mm});
            skLineSegment(sketch, "E79.1.0.7", {"start": v(1006.25, 534) * mm, "end": v(1306.25, 534) * mm});
            skLineSegment(sketch, "E79.2.0.0", {"start": v(1992.5, 534) * mm, "end": v(1992.5, 834) * mm});
            skLineSegment(sketch, "E79.2.0.1", {"start": v(1992.5, 30) * mm, "end": v(1992.5, 330) * mm});
            skLineSegment(sketch, "E79.2.0.2", {"start": v(1692.5, 834) * mm, "end": v(1992.5, 834) * mm});
            skLineSegment(sketch, "E79.2.0.3", {"start": v(1692.5, 534) * mm, "end": v(1692.5, 834) * mm});
            skLineSegment(sketch, "E79.2.0.4", {"start": v(1692.5, 30) * mm, "end": v(1992.5, 30) * mm});
            skLineSegment(sketch, "E79.2.0.5", {"start": v(1692.5, 330) * mm, "end": v(1992.5, 330) * mm});
            skLineSegment(sketch, "E79.2.0.6", {"start": v(1692.5, 30) * mm, "end": v(1692.5, 330) * mm});
            skLineSegment(sketch, "E79.2.0.7", {"start": v(1692.5, 534) * mm, "end": v(1992.5, 534) * mm});
            skLineSegment(sketch, "E79.3.0.0", {"start": v(2678.75, 534) * mm, "end": v(2678.75, 834) * mm});
            skLineSegment(sketch, "E79.3.0.1", {"start": v(2678.75, 30) * mm, "end": v(2678.75, 330) * mm});
            skLineSegment(sketch, "E79.3.0.2", {"start": v(2378.75, 834) * mm, "end": v(2678.75, 834) * mm});
            skLineSegment(sketch, "E79.3.0.3", {"start": v(2378.75, 534) * mm, "end": v(2378.75, 834) * mm});
            skLineSegment(sketch, "E79.3.0.4", {"start": v(2378.75, 30) * mm, "end": v(2678.75, 30) * mm});
            skLineSegment(sketch, "E79.3.0.5", {"start": v(2378.75, 330) * mm, "end": v(2678.75, 330) * mm});
            skLineSegment(sketch, "E79.3.0.6", {"start": v(2378.75, 30) * mm, "end": v(2378.75, 330) * mm});
            skLineSegment(sketch, "E79.3.0.7", {"start": v(2378.75, 534) * mm, "end": v(2678.75, 534) * mm});
            skLineSegment(sketch, "E79.4.0.0", {"start": v(3365, 534) * mm, "end": v(3365, 834) * mm});
            skLineSegment(sketch, "E79.4.0.1", {"start": v(3365, 30) * mm, "end": v(3365, 330) * mm});
            skLineSegment(sketch, "E79.4.0.2", {"start": v(3065, 834) * mm, "end": v(3365, 834) * mm});
            skLineSegment(sketch, "E79.4.0.3", {"start": v(3065, 534) * mm, "end": v(3065, 834) * mm});
            skLineSegment(sketch, "E79.4.0.4", {"start": v(3065, 30) * mm, "end": v(3365, 30) * mm});
            skLineSegment(sketch, "E79.4.0.5", {"start": v(3065, 330) * mm, "end": v(3365, 330) * mm});
            skLineSegment(sketch, "E79.4.0.6", {"start": v(3065, 30) * mm, "end": v(3065, 330) * mm});
            skLineSegment(sketch, "E79.4.0.7", {"start": v(3065, 534) * mm, "end": v(3365, 534) * mm});
            skLineSegment(sketch, "E79.direction1", {"start": v(320, 30) * mm, "end": v(1006.25, 30) * mm, "construction": true});
            skLineSegment(sketch, "E80.bottom", {"start": v(320, 2000) * mm, "end": v(620, 2000) * mm});
            skLineSegment(sketch, "E80.top", {"start": v(320, 1850) * mm, "end": v(620, 1850) * mm});
            skLineSegment(sketch, "E80.left", {"start": v(320, 2000) * mm, "end": v(320, 1850) * mm});
            skLineSegment(sketch, "E80.right", {"start": v(620, 2000) * mm, "end": v(620, 1850) * mm});
            skLineSegment(sketch, "E81.1.0.0", {"start": v(1006.25, 2000) * mm, "end": v(1006.25, 1850) * mm});
            skLineSegment(sketch, "E81.1.0.1", {"start": v(1306.25, 2305) * mm, "end": v(1306.25, 2005) * mm});
            skLineSegment(sketch, "E81.1.0.2", {"start": v(1306.25, 2000) * mm, "end": v(1306.25, 1850) * mm});
            skLineSegment(sketch, "E81.1.0.3", {"start": v(1006.25, 2005) * mm, "end": v(1306.25, 2005) * mm});
            skLineSegment(sketch, "E81.1.0.4", {"start": v(1006.25, 2000) * mm, "end": v(1306.25, 2000) * mm});
            skLineSegment(sketch, "E81.1.0.5", {"start": v(1006.25, 2305) * mm, "end": v(1006.25, 2005) * mm});
            skLineSegment(sketch, "E81.1.0.6", {"start": v(1006.25, 2305) * mm, "end": v(1306.25, 2305) * mm});
            skLineSegment(sketch, "E81.1.0.7", {"start": v(1006.25, 1850) * mm, "end": v(1306.25, 1850) * mm});
            skLineSegment(sketch, "E81.2.0.0", {"start": v(1692.5, 2000) * mm, "end": v(1692.5, 1850) * mm});
            skLineSegment(sketch, "E81.2.0.1", {"start": v(1992.5, 2305) * mm, "end": v(1992.5, 2005) * mm});
            skLineSegment(sketch, "E81.2.0.2", {"start": v(1992.5, 2000) * mm, "end": v(1992.5, 1850) * mm});
            skLineSegment(sketch, "E81.2.0.3", {"start": v(1692.5, 2005) * mm, "end": v(1992.5, 2005) * mm});
            skLineSegment(sketch, "E81.2.0.4", {"start": v(1692.5, 2000) * mm, "end": v(1992.5, 2000) * mm});
            skLineSegment(sketch, "E81.2.0.5", {"start": v(1692.5, 2305) * mm, "end": v(1692.5, 2005) * mm});
            skLineSegment(sketch, "E81.2.0.6", {"start": v(1692.5, 2305) * mm, "end": v(1992.5, 2305) * mm});
            skLineSegment(sketch, "E81.2.0.7", {"start": v(1692.5, 1850) * mm, "end": v(1992.5, 1850) * mm});
            skLineSegment(sketch, "E81.3.0.0", {"start": v(2378.75, 2000) * mm, "end": v(2378.75, 1850) * mm});
            skLineSegment(sketch, "E81.3.0.1", {"start": v(2678.75, 2305) * mm, "end": v(2678.75, 2005) * mm});
            skLineSegment(sketch, "E81.3.0.2", {"start": v(2678.75, 2000) * mm, "end": v(2678.75, 1850) * mm});
            skLineSegment(sketch, "E81.3.0.3", {"start": v(2378.75, 2005) * mm, "end": v(2678.75, 2005) * mm});
            skLineSegment(sketch, "E81.3.0.4", {"start": v(2378.75, 2000) * mm, "end": v(2678.75, 2000) * mm});
            skLineSegment(sketch, "E81.3.0.5", {"start": v(2378.75, 2305) * mm, "end": v(2378.75, 2005) * mm});
            skLineSegment(sketch, "E81.3.0.6", {"start": v(2378.75, 2305) * mm, "end": v(2678.75, 2305) * mm});
            skLineSegment(sketch, "E81.3.0.7", {"start": v(2378.75, 1850) * mm, "end": v(2678.75, 1850) * mm});
            skLineSegment(sketch, "E81.4.0.0", {"start": v(3065, 2000) * mm, "end": v(3065, 1850) * mm});
            skLineSegment(sketch, "E81.4.0.1", {"start": v(3365, 2305) * mm, "end": v(3365, 2005) * mm});
            skLineSegment(sketch, "E81.4.0.2", {"start": v(3365, 2000) * mm, "end": v(3365, 1850) * mm});
            skLineSegment(sketch, "E81.4.0.3", {"start": v(3065, 2005) * mm, "end": v(3365, 2005) * mm});
            skLineSegment(sketch, "E81.4.0.4", {"start": v(3065, 2000) * mm, "end": v(3365, 2000) * mm});
            skLineSegment(sketch, "E81.4.0.5", {"start": v(3065, 2305) * mm, "end": v(3065, 2005) * mm});
            skLineSegment(sketch, "E81.4.0.6", {"start": v(3065, 2305) * mm, "end": v(3365, 2305) * mm});
            skLineSegment(sketch, "E81.4.0.7", {"start": v(3065, 1850) * mm, "end": v(3365, 1850) * mm});
            skLineSegment(sketch, "E81.direction1", {"start": v(320, 1850) * mm, "end": v(1006.25, 1850) * mm, "construction": true});
            skLineSegment(sketch, "E82.bottom", {"start": v(320, 514) * mm, "end": v(620, 514) * mm});
            skLineSegment(sketch, "E82.top", {"start": v(320, 364) * mm, "end": v(620, 364) * mm});
            skLineSegment(sketch, "E82.left", {"start": v(320, 514) * mm, "end": v(320, 364) * mm});
            skLineSegment(sketch, "E82.right", {"start": v(620, 514) * mm, "end": v(620, 364) * mm});
            skLineSegment(sketch, "E83.1.0.0", {"start": v(1306.25, 514) * mm, "end": v(1306.25, 364) * mm});
            skLineSegment(sketch, "E83.1.0.1", {"start": v(1006.25, 514) * mm, "end": v(1306.25, 514) * mm});
            skLineSegment(sketch, "E83.1.0.2", {"start": v(1006.25, 514) * mm, "end": v(1006.25, 364) * mm});
            skLineSegment(sketch, "E83.1.0.3", {"start": v(1006.25, 364) * mm, "end": v(1306.25, 364) * mm});
            skLineSegment(sketch, "E83.2.0.0", {"start": v(1992.5, 514) * mm, "end": v(1992.5, 364) * mm});
            skLineSegment(sketch, "E83.2.0.1", {"start": v(1692.5, 514) * mm, "end": v(1992.5, 514) * mm});
            skLineSegment(sketch, "E83.2.0.2", {"start": v(1692.5, 514) * mm, "end": v(1692.5, 364) * mm});
            skLineSegment(sketch, "E83.2.0.3", {"start": v(1692.5, 364) * mm, "end": v(1992.5, 364) * mm});
            skLineSegment(sketch, "E83.3.0.0", {"start": v(2678.75, 514) * mm, "end": v(2678.75, 364) * mm});
            skLineSegment(sketch, "E83.3.0.1", {"start": v(2378.75, 514) * mm, "end": v(2678.75, 514) * mm});
            skLineSegment(sketch, "E83.3.0.2", {"start": v(2378.75, 514) * mm, "end": v(2378.75, 364) * mm});
            skLineSegment(sketch, "E83.3.0.3", {"start": v(2378.75, 364) * mm, "end": v(2678.75, 364) * mm});
            skLineSegment(sketch, "E83.4.0.0", {"start": v(3365, 514) * mm, "end": v(3365, 364) * mm});
            skLineSegment(sketch, "E83.4.0.1", {"start": v(3065, 514) * mm, "end": v(3365, 514) * mm});
            skLineSegment(sketch, "E83.4.0.2", {"start": v(3065, 514) * mm, "end": v(3065, 364) * mm});
            skLineSegment(sketch, "E83.4.0.3", {"start": v(3065, 364) * mm, "end": v(3365, 364) * mm});
            skLineSegment(sketch, "E83.direction1", {"start": v(320, 364) * mm, "end": v(1006.25, 364) * mm, "construction": true});
            skSolve(sketch);
        }
        {
            var Q0;
            Q0 = qSketchRegion(id + "F32", true);
            extrude(context, id + "F33", {"entities" : qUnion([Q0]), "depth" : 42 * mm, "offsetDistance" : 25 * mm});
        }
    });
